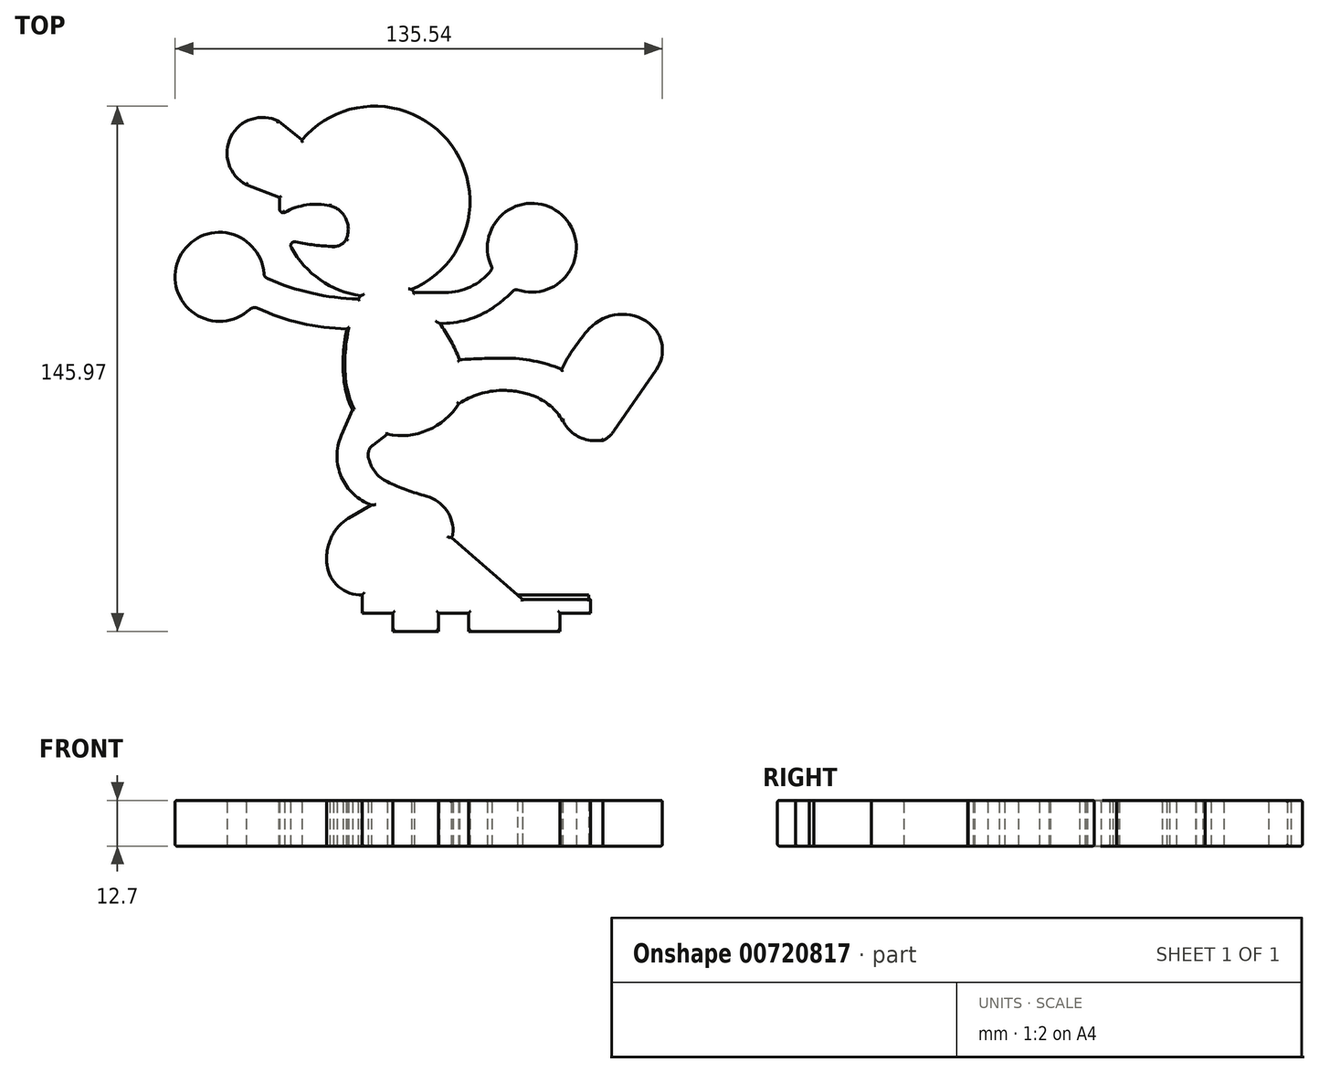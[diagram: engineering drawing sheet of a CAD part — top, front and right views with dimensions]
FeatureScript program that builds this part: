
annotation { "Feature Type Name" : "Feature", "Feature Type Description" : "" }
export const myFeature = defineFeature(function(context is Context, id is Id, definition is map)
    precondition{}
    {
        {
            var Q0;
            Q0=qCreatedBy(makeId("Top.planeOp"),FACE);
            var sketch = newSketch(context, id + "F0", { "sketchPlane" : qUnion([Q0])});
            skArc(sketch, "E0", {"start": v(-43.33, 22.04) * mm, "mid": v(-67.17, 25.66) * mm, "end": v(-47.24, 12.1) * mm});
            skArc(sketch, "E1", {"start": v(27.14, 17.54) * mm, "mid": v(39.52, 38.36) * mm, "end": v(19.95, 24.08) * mm});
            skArc(sketch, "E2", {"start": v(-42.38, 20.68) * mm, "mid": v(-30.02, 16.59) * mm, "end": v(-17.1, 14.96) * mm});
            skArc(sketch, "E3", {"start": v(-45.14, 12.43) * mm, "mid": v(-33, 8.29) * mm, "end": v(-20.29, 6.67) * mm});
            skEllipticalArc(sketch, "E4", {});
            skPoint(sketch, "E5", {"position": v(-18.69, -15.72) * mm});
            skLineSegment(sketch, "E6", {"start": v(-17.1, 14.96) * mm, "end": v(-16.42, 15.86) * mm});
            skArc(sketch, "E7", {"start": v(-39, 43.2) * mm, "mid": v(-39.02, 41.5) * mm, "end": v(-38.93, 39.8) * mm});
            skLineSegment(sketch, "E8", {"start": v(-32.74, 59.21) * mm, "end": v(-39.25, 64.38) * mm});
            skLineSegment(sketch, "E9", {"start": v(-39, 43.2) * mm, "end": v(-48.2, 46.76) * mm});
            skArc(sketch, "E10", {"start": v(-39.25, 64.38) * mm, "mid": v(-52.53, 60.05) * mm, "end": v(-48.2, 46.76) * mm});
            skLineSegment(sketch, "E11", {"start": v(-2.3, 17.63) * mm, "end": v(-1.5, 16.75) * mm});
            skArc(sketch, "E12.trimOffspring", {"start": v(-2.3, 17.63) * mm, "mid": v(8.85, 57.73) * mm, "end": v(-32.74, 59.21) * mm});
            skArc(sketch, "E13", {"start": v(-24.96, 40.92) * mm, "mid": v(-31.45, 41.14) * mm, "end": v(-37.59, 39.03) * mm});
            skArc(sketch, "E14", {"start": v(-20.44, 31.63) * mm, "mid": v(-20.53, 37.33) * mm, "end": v(-24.96, 40.92) * mm});
            skArc(sketch, "E15", {"start": v(-23.99, 29.6) * mm, "mid": v(-21.9, 30.07) * mm, "end": v(-20.44, 31.63) * mm});
            skArc(sketch, "E16", {"start": v(-34.52, 30.88) * mm, "mid": v(-29.29, 29.99) * mm, "end": v(-23.99, 29.6) * mm});
            skArc(sketch, "E17.trimOffspring", {"start": v(-35.73, 29.26) * mm, "mid": v(-27.64, 20.3) * mm, "end": v(-16.42, 15.86) * mm});
            skArc(sketch, "E18", {"start": v(-34.52, 30.88) * mm, "mid": v(-35.65, 30.46) * mm, "end": v(-35.73, 29.26) * mm});
            skArc(sketch, "E19", {"start": v(-38.93, 39.8) * mm, "mid": v(-38.42, 39.04) * mm, "end": v(-37.5, 39.09) * mm});
            skLineSegment(sketch, "E20", {"start": v(-1.5, 16.75) * mm, "end": v(7.07, 16.75) * mm});
            skArc(sketch, "E21", {"start": v(7.07, 16.75) * mm, "mid": v(14.13, 18.36) * mm, "end": v(19.8, 22.86) * mm});
            skArc(sketch, "E22", {"start": v(19.8, 22.86) * mm, "mid": v(20.04, 23.45) * mm, "end": v(19.95, 24.08) * mm});
            skArc(sketch, "E23", {"start": v(-43.33, 22.04) * mm, "mid": v(-43.04, 21.23) * mm, "end": v(-42.38, 20.68) * mm});
            skPoint(sketch, "E24.orphan", {"position": v(-43.3, 21.1) * mm});
            skArc(sketch, "E25", {"start": v(-45.14, 12.43) * mm, "mid": v(-46.24, 12.58) * mm, "end": v(-47.24, 12.1) * mm});
            skPoint(sketch, "E26.orphan", {"position": v(-46.36, 13) * mm});
            skLineSegment(sketch, "E27", {"start": v(-18.69, -15.72) * mm, "end": v(-21.82, -23) * mm});
            skArc(sketch, "E28", {"start": v(-21.82, -23) * mm, "mid": v(-21.8, -34.48) * mm, "end": v(-13.38, -42.3) * mm});
            skArc(sketch, "E29", {"start": v(-12.97, -25.6) * mm, "mid": v(-14.1, -27.07) * mm, "end": v(-14.28, -28.92) * mm});
            skLineSegment(sketch, "E30", {"start": v(-9.03, -22.63) * mm, "end": v(-12.97, -25.6) * mm});
            skArc(sketch, "E31", {"start": v(-14.28, -28.92) * mm, "mid": v(-12.49, -33) * mm, "end": v(-9.03, -35.82) * mm});
            skArc(sketch, "E32", {"start": v(-9.03, -35.82) * mm, "mid": v(-3.66, -38.09) * mm, "end": v(1.9, -39.85) * mm});
            skArc(sketch, "E33", {"start": v(9.21, -50.49) * mm, "mid": v(7.52, -43.82) * mm, "end": v(1.9, -39.85) * mm});
            skLineSegment(sketch, "E34", {"start": v(8.75, -51.34) * mm, "end": v(-6.07, -63.4) * mm});
            skArc(sketch, "E35", {"start": v(-15.93, -67.24) * mm, "mid": v(-10.7, -66.09) * mm, "end": v(-6.07, -63.4) * mm});
            skArc(sketch, "E36", {"start": v(-25.81, -58.87) * mm, "mid": v(-22.55, -65.04) * mm, "end": v(-15.93, -67.24) * mm});
            skArc(sketch, "E37", {"start": v(-24.09, -50.35) * mm, "mid": v(-25.6, -54.48) * mm, "end": v(-25.81, -58.87) * mm});
            skLineSegment(sketch, "E38", {"start": v(-19.74, -45.94) * mm, "end": v(-13.38, -42.3) * mm});
            skArc(sketch, "E39", {"start": v(-19.74, -45.94) * mm, "mid": v(-22.22, -47.85) * mm, "end": v(-24.09, -50.35) * mm});
            skArc(sketch, "E40", {"start": v(-9.03, -22.63) * mm, "mid": v(2.23, -21.5) * mm, "end": v(10.87, -14.17) * mm});
            skArc(sketch, "E41", {"start": v(22.9, -10.44) * mm, "mid": v(16.62, -11.44) * mm, "end": v(10.87, -14.17) * mm});
            skArc(sketch, "E42", {"start": v(31.6, -11.96) * mm, "mid": v(27.33, -10.8) * mm, "end": v(22.9, -10.44) * mm});
            skArc(sketch, "E43", {"start": v(39.8, -18.87) * mm, "mid": v(36.3, -14.71) * mm, "end": v(31.6, -11.96) * mm});
            skArc(sketch, "E44", {"start": v(39.8, -18.87) * mm, "mid": v(42.95, -22.56) * mm, "end": v(47.47, -24.32) * mm});
            skArc(sketch, "E45", {"start": v(47.47, -24.32) * mm, "mid": v(49.23, -24.44) * mm, "end": v(50.99, -24.32) * mm});
            skArc(sketch, "E46", {"start": v(20.34, 12.52) * mm, "mid": v(23.32, 14.77) * mm, "end": v(26.08, 17.3) * mm});
            skArc(sketch, "E47", {"start": v(5.5, 8.21) * mm, "mid": v(13.26, 9.19) * mm, "end": v(20.34, 12.52) * mm});
            skArc(sketch, "E48", {"start": v(11.07, -1.9) * mm, "mid": v(8.64, 3.35) * mm, "end": v(5.5, 8.21) * mm});
            skArc(sketch, "E49", {"start": v(23.58, -1.46) * mm, "mid": v(17.32, -1.59) * mm, "end": v(11.07, -1.9) * mm});
            skArc(sketch, "E50", {"start": v(39.46, -4.56) * mm, "mid": v(31.67, -2.23) * mm, "end": v(23.58, -1.46) * mm});
            skArc(sketch, "E51", {"start": v(47.18, 6.71) * mm, "mid": v(42.93, 1.34) * mm, "end": v(39.46, -4.56) * mm});
            skArc(sketch, "E52", {"start": v(63.86, 8.16) * mm, "mid": v(55.24, 10.7) * mm, "end": v(47.18, 6.71) * mm});
            skArc(sketch, "E53", {"start": v(65.84, -4.62) * mm, "mid": v(67.4, 2.16) * mm, "end": v(63.86, 8.16) * mm});
            skArc(sketch, "E54", {"start": v(50.99, -24.32) * mm, "mid": v(52.68, -23.22) * mm, "end": v(54.03, -21.71) * mm});
            skLineSegment(sketch, "E55", {"start": v(65.84, -4.62) * mm, "end": v(54.03, -21.71) * mm});
            skPoint(sketch, "E56.visualSharp", {"position": v(9.14, -51.02) * mm});
            skArc(sketch, "E56.filletArc", {"start": v(8.75, -51.34) * mm, "mid": v(9.06, -50.96) * mm, "end": v(9.21, -50.49) * mm});
            skLineSegment(sketch, "E57", {"start": v(8.75, -51.34) * mm, "end": v(27.15, -67.24) * mm});
            skLineSegment(sketch, "E58", {"start": v(27.15, -67.24) * mm, "end": v(47.47, -67.24) * mm});
            skLineSegment(sketch, "E59", {"start": v(47.47, -67.24) * mm, "end": v(47.47, -72.32) * mm});
            skLineSegment(sketch, "E60", {"start": v(-15.93, -67.24) * mm, "end": v(-15.93, -72.32) * mm});
            skLineSegment(sketch, "E61", {"start": v(-15.93, -72.32) * mm, "end": v(-7.5, -72.32) * mm});
            skLineSegment(sketch, "E62", {"start": v(-7.5, -72.32) * mm, "end": v(-7.5, -77.4) * mm});
            skLineSegment(sketch, "E63", {"start": v(-7.5, -77.4) * mm, "end": v(5.2, -77.4) * mm});
            skLineSegment(sketch, "E64", {"start": v(5.2, -77.4) * mm, "end": v(5.2, -72.32) * mm});
            skLineSegment(sketch, "E65", {"start": v(5.2, -72.32) * mm, "end": v(13.64, -72.32) * mm});
            skLineSegment(sketch, "E66", {"start": v(13.64, -72.32) * mm, "end": v(13.64, -77.4) * mm});
            skLineSegment(sketch, "E67", {"start": v(13.64, -77.4) * mm, "end": v(39.04, -77.4) * mm});
            skLineSegment(sketch, "E68", {"start": v(39.04, -77.4) * mm, "end": v(39.04, -72.32) * mm});
            skLineSegment(sketch, "E69", {"start": v(39.04, -72.32) * mm, "end": v(47.47, -72.32) * mm});
            skPoint(sketch, "E70.visualSharp", {"position": v(26.54, 17.76) * mm});
            skArc(sketch, "E70.filletArc", {"start": v(27.14, 17.54) * mm, "mid": v(26.57, 17.57) * mm, "end": v(26.08, 17.3) * mm});
            skLineSegment(sketch, "E71", {"start": v(-15.93, -72.32) * mm, "end": v(47.47, -72.32) * mm});
            skLineSegment(sketch, "E72", {"start": v(27.15, -67.24) * mm, "end": v(28.62, -68.5) * mm});
            skLineSegment(sketch, "E73", {"start": v(28.62, -68.5) * mm, "end": v(47.47, -68.5) * mm});
            skPoint(sketch, "E73.endSnap0", {"position": v(47.47, -69.78) * mm});
            skLineSegment(sketch, "E74", {"start": v(46.96, -67.24) * mm, "end": v(46.96, -68.5) * mm});
            const initialGuessF0  = {"E4": [-0.011952799744904041, 0.001971718389540909, -0.13325470895855734, -0.9910818243416486, 0.020995345255248873, 0.009018086329154872, 4.542475182199663, 5.783986003179863]};
            skSetInitialGuess(sketch, initialGuessF0);
            skSolve(sketch);
        }
        {
            var Q0;
            Q0=makeQuery(id+"F0.imprint","IMPRINT",FACE,{"disambiguationData":[TD([[makeQuery(id+"F0.imprint","IMPRINT",EDGE,{"derivedFrom":sQuery(id+"F0.wireOp",EDGE,"E0")}),1.0]])]});
            var Q1;
            Q1=makeQuery(id+"F0.imprint","IMPRINT",FACE,{"disambiguationData":[TD([[makeQuery(id+"F0.imprint","IMPRINT",EDGE,{"derivedFrom":sQuery(id+"F0.wireOp",EDGE,"E34")}),1.0]])]});
            var Q2;
            {var subQ0=sQuery(id+"F0.wireOp",EDGE,"E62");Q2=makeQuery(id+"F0.imprint","IMPRINT",FACE,{"disambiguationData":[TD([[makeQuery(id+"F0.imprint","IMPRINT",EDGE,{"derivedFrom":subQ0}),1.0]])]});}
            var Q3;
            {var subQ0=sQuery(id+"F0.wireOp",EDGE,"E66");Q3=makeQuery(id+"F0.imprint","IMPRINT",FACE,{"disambiguationData":[TD([[makeQuery(id+"F0.imprint","IMPRINT",EDGE,{"derivedFrom":subQ0}),1.0]])]});}
            extrude(context, id + "F1", {"entities" : qUnion([Q0, Q1, Q2, Q3]), "depth" : 12.7 * mm, "offsetDistance" : 25.4 * mm});
        }
        {
            var Q0;
            Q0=makeQuery(id+"F1.opExtrude","CAP_FACE",FACE,{"disambiguationData":[OSD([sQuery(id+"F0.wireOp",EDGE,"E0"),sQuery(id+"F0.wireOp",EDGE,"E1"),sQuery(id+"F0.wireOp",EDGE,"E2"),sQuery(id+"F0.wireOp",EDGE,"E3"),sQuery(id+"F0.wireOp",EDGE,"E4"),sQuery(id+"F0.wireOp",EDGE,"E6"),sQuery(id+"F0.wireOp",EDGE,"E7"),sQuery(id+"F0.wireOp",EDGE,"E8"),sQuery(id+"F0.wireOp",EDGE,"E9"),sQuery(id+"F0.wireOp",EDGE,"E10"),sQuery(id+"F0.wireOp",EDGE,"E11"),sQuery(id+"F0.wireOp",EDGE,"E12.trimOffspring"),sQuery(id+"F0.wireOp",EDGE,"E13"),sQuery(id+"F0.wireOp",EDGE,"E14"),sQuery(id+"F0.wireOp",EDGE,"E15"),sQuery(id+"F0.wireOp",EDGE,"E16"),sQuery(id+"F0.wireOp",EDGE,"E17.trimOffspring"),sQuery(id+"F0.wireOp",EDGE,"E18"),sQuery(id+"F0.wireOp",EDGE,"E19"),sQuery(id+"F0.wireOp",EDGE,"E20"),sQuery(id+"F0.wireOp",EDGE,"E21"),sQuery(id+"F0.wireOp",EDGE,"E22"),sQuery(id+"F0.wireOp",EDGE,"E23"),sQuery(id+"F0.wireOp",EDGE,"E25"),sQuery(id+"F0.wireOp",EDGE,"E27"),sQuery(id+"F0.wireOp",EDGE,"E28"),sQuery(id+"F0.wireOp",EDGE,"E29"),sQuery(id+"F0.wireOp",EDGE,"E30"),sQuery(id+"F0.wireOp",EDGE,"E31"),sQuery(id+"F0.wireOp",EDGE,"E32"),sQuery(id+"F0.wireOp",EDGE,"E33"),sQuery(id+"F0.wireOp",EDGE,"E36"),sQuery(id+"F0.wireOp",EDGE,"E37"),sQuery(id+"F0.wireOp",EDGE,"E38"),sQuery(id+"F0.wireOp",EDGE,"E39"),sQuery(id+"F0.wireOp",EDGE,"E40"),sQuery(id+"F0.wireOp",EDGE,"E41"),sQuery(id+"F0.wireOp",EDGE,"E42"),sQuery(id+"F0.wireOp",EDGE,"E43"),sQuery(id+"F0.wireOp",EDGE,"E44"),sQuery(id+"F0.wireOp",EDGE,"E45"),sQuery(id+"F0.wireOp",EDGE,"E46"),sQuery(id+"F0.wireOp",EDGE,"E47"),sQuery(id+"F0.wireOp",EDGE,"E48"),sQuery(id+"F0.wireOp",EDGE,"E49"),sQuery(id+"F0.wireOp",EDGE,"E50"),sQuery(id+"F0.wireOp",EDGE,"E51"),sQuery(id+"F0.wireOp",EDGE,"E52"),sQuery(id+"F0.wireOp",EDGE,"E53"),sQuery(id+"F0.wireOp",EDGE,"E54"),sQuery(id+"F0.wireOp",EDGE,"E55"),sQuery(id+"F0.wireOp",EDGE,"E56.filletArc"),sQuery(id+"F0.wireOp",EDGE,"E57"),sQuery(id+"F0.wireOp",EDGE,"E58"),sQuery(id+"F0.wireOp",EDGE,"E59"),sQuery(id+"F0.wireOp",EDGE,"E60"),sQuery(id+"F0.wireOp",EDGE,"E61"),sQuery(id+"F0.wireOp",EDGE,"E62"),sQuery(id+"F0.wireOp",EDGE,"E63"),sQuery(id+"F0.wireOp",EDGE,"E64"),sQuery(id+"F0.wireOp",EDGE,"E65"),sQuery(id+"F0.wireOp",EDGE,"E66"),sQuery(id+"F0.wireOp",EDGE,"E67"),sQuery(id+"F0.wireOp",EDGE,"E68"),sQuery(id+"F0.wireOp",EDGE,"E69")])],"isStart":false});
            var Q1;
            Q1=makeQuery(id+"F1.opExtrude","CAP_FACE",FACE,{"disambiguationData":[OSD([sQuery(id+"F0.wireOp",EDGE,"E0"),sQuery(id+"F0.wireOp",EDGE,"E1"),sQuery(id+"F0.wireOp",EDGE,"E2"),sQuery(id+"F0.wireOp",EDGE,"E3"),sQuery(id+"F0.wireOp",EDGE,"E4"),sQuery(id+"F0.wireOp",EDGE,"E6"),sQuery(id+"F0.wireOp",EDGE,"E7"),sQuery(id+"F0.wireOp",EDGE,"E8"),sQuery(id+"F0.wireOp",EDGE,"E9"),sQuery(id+"F0.wireOp",EDGE,"E10"),sQuery(id+"F0.wireOp",EDGE,"E11"),sQuery(id+"F0.wireOp",EDGE,"E12.trimOffspring"),sQuery(id+"F0.wireOp",EDGE,"E13"),sQuery(id+"F0.wireOp",EDGE,"E14"),sQuery(id+"F0.wireOp",EDGE,"E15"),sQuery(id+"F0.wireOp",EDGE,"E16"),sQuery(id+"F0.wireOp",EDGE,"E17.trimOffspring"),sQuery(id+"F0.wireOp",EDGE,"E18"),sQuery(id+"F0.wireOp",EDGE,"E19"),sQuery(id+"F0.wireOp",EDGE,"E20"),sQuery(id+"F0.wireOp",EDGE,"E21"),sQuery(id+"F0.wireOp",EDGE,"E22"),sQuery(id+"F0.wireOp",EDGE,"E23"),sQuery(id+"F0.wireOp",EDGE,"E25"),sQuery(id+"F0.wireOp",EDGE,"E27"),sQuery(id+"F0.wireOp",EDGE,"E28"),sQuery(id+"F0.wireOp",EDGE,"E29"),sQuery(id+"F0.wireOp",EDGE,"E30"),sQuery(id+"F0.wireOp",EDGE,"E31"),sQuery(id+"F0.wireOp",EDGE,"E32"),sQuery(id+"F0.wireOp",EDGE,"E33"),sQuery(id+"F0.wireOp",EDGE,"E36"),sQuery(id+"F0.wireOp",EDGE,"E37"),sQuery(id+"F0.wireOp",EDGE,"E38"),sQuery(id+"F0.wireOp",EDGE,"E39"),sQuery(id+"F0.wireOp",EDGE,"E40"),sQuery(id+"F0.wireOp",EDGE,"E41"),sQuery(id+"F0.wireOp",EDGE,"E42"),sQuery(id+"F0.wireOp",EDGE,"E43"),sQuery(id+"F0.wireOp",EDGE,"E44"),sQuery(id+"F0.wireOp",EDGE,"E45"),sQuery(id+"F0.wireOp",EDGE,"E46"),sQuery(id+"F0.wireOp",EDGE,"E47"),sQuery(id+"F0.wireOp",EDGE,"E48"),sQuery(id+"F0.wireOp",EDGE,"E49"),sQuery(id+"F0.wireOp",EDGE,"E50"),sQuery(id+"F0.wireOp",EDGE,"E51"),sQuery(id+"F0.wireOp",EDGE,"E52"),sQuery(id+"F0.wireOp",EDGE,"E53"),sQuery(id+"F0.wireOp",EDGE,"E54"),sQuery(id+"F0.wireOp",EDGE,"E55"),sQuery(id+"F0.wireOp",EDGE,"E56.filletArc"),sQuery(id+"F0.wireOp",EDGE,"E57"),sQuery(id+"F0.wireOp",EDGE,"E58"),sQuery(id+"F0.wireOp",EDGE,"E59"),sQuery(id+"F0.wireOp",EDGE,"E60"),sQuery(id+"F0.wireOp",EDGE,"E61"),sQuery(id+"F0.wireOp",EDGE,"E62"),sQuery(id+"F0.wireOp",EDGE,"E63"),sQuery(id+"F0.wireOp",EDGE,"E64"),sQuery(id+"F0.wireOp",EDGE,"E65"),sQuery(id+"F0.wireOp",EDGE,"E66"),sQuery(id+"F0.wireOp",EDGE,"E67"),sQuery(id+"F0.wireOp",EDGE,"E68"),sQuery(id+"F0.wireOp",EDGE,"E69")])],"isStart":true});
            fillet(context, id + "F2", {"entities" : qUnion([Q0, Q1]), "radius" : 0.5 * mm, "tangentPropagation" : true, "allowEdgeOverflow" : false});
        }
        {
            var Q0;
            {var subQ0=sQuery(id+"F0.wireOp",EDGE,"E72");Q0=makeQuery(id+"F0.imprint","IMPRINT",FACE,{"disambiguationData":[TD([[makeQuery(id+"F0.imprint","IMPRINT",EDGE,{"derivedFrom":subQ0}),1.0]])]});}
            extrude(context, id + "F3", {"entities" : qUnion([Q0]), "depth" : 12.7 * mm, "offsetDistance" : 25.4 * mm});
        }
    });
